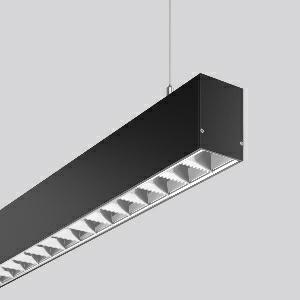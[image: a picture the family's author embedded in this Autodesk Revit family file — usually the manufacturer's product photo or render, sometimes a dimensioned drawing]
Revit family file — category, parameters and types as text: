
# Revit family: less_is_more_50_312336_003_76_c688
name_source: partatom
category: Lighting Fixtures
units: mm (PartAtom-declared; Revit-internal decimal feet)

## family parameters
Cut with Voids When Loaded = No
Host = Face
Light Source = No
Part Type = Normal
Room Calculation Point = No
Round Connector Dimension = Use Diameter
Shared = No

## types (1)
- LESS IS MORE 50 (1 x LED Modul 830, 3350 lm, 3000)
    Apparent Load = 28 VA
    CIE Flux Codes = 95 100 100 100 100
    Color Rendering = 80
    Color Temperature = 3000
    Default Elevation = 1800 mm
    Description = Series: LESS IS MORE 50
Linear pendant luminaire for aesthetically sophisticated lighting. Housing: extruded aluminium profile, powder-coated. End cap aluminium powder-coated. Canopy made of aluminium, powder-coated. Alea optical system: Reflector structure (ABS, Aluminium-coated, highly polished) with integrated diffuser made of non-yellowing plastic (PMMA) opal for glare-free light at the workstation (screen-compliant according to EN 12464-1). Direct light emission. Suitable for pendant. 2-point steel cable suspension freely positionable and infinitely height-adjustable. Special lengths available on request. LED unit with integrated converter interchangeable and removable. Suitable for through-wiring. With sensors or as a safety luminaire on request. 
Colour: deep black, matt (RAL 9005)
Length: 1127 mm
Width: 57 mm
Height: 75 mm
Suspension length: 2000 mm
Lamp: LED
Socket: without socket
Colour temperature: 3000K
Colour rendering index (CRI): 80
System power: 28 W
Rated luminous flux: 3350 lm
Luminous efficiency: 120 lm/W
Control gear: Converter, dimmable, DALI
Protection class: I
Type of protection: IP 20
    Height = 75 mm
    Lamp = 1 x LED Modul 830
    Lamp Light Flux = 3350 lm
    Lamp count = 1
    Length = 1127 mm
    Lifetime = 50000 h
    Luminous efficacy = 120 lm/W
    Manufacturer = RZB
    ModVariant = No
    Model = 312336.003.76
    Mounting Place = Ceiling
    Mounting Type = Pendant
    Number of Poles = 1
    OnlyDefault = Yes
    Power Factor = 1
    Product Name = LESS IS MORE 50
    Product group = Pendant LED linear luminaires
    ProductGroupID = 907
    Protection Class = Protection class I
    Protection Degree = IP 20
    RLX_Detail_Level = 1
    RLX_Emergency_Light_Flux = 0 lm
    RLX_Emergency_Type = 0
    RLX_Emergency_Type_DB = No
    RlxData = <blob elided: 39597 chars, md5=fdbde10d>
    Socket = socket
    Standby Power = 0 W
    System Light Flux = 3350 lm
    System Power = 28 W
    Type Comments = Product without accessories
    Type Image = 312342.003.jpg
    URL = http://relux.com
    VarID = ---
    Voltage = 230 V
    Voltage Range = 220-240 V
    Weight = 0.00 kg
    Width = 57 mm

## geometry (parser evidence)
native form markers: Blend x4, Sweep x10
no freeform markers — native parametric forms only
